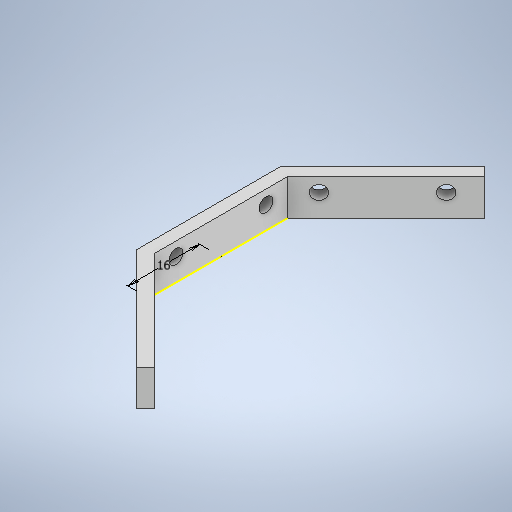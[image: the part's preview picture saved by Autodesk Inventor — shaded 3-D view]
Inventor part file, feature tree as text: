
AUTODESK INVENTOR PART (.ipt)
format: ipt  version: 2025.1 (Build 291241020, 241B)  size: 315,904 bytes
history: native  units: in
note: dims shown in document units (in); Inventor stores cm internally (conversion verified against a paired STEP export)
features: sketch x5, extrude x4
ambient origin geometry x8: Origin, YZ Plane, XZ Plane, XY Plane, X Axis, Y Axis, Z Axis, Center Point
bodies: Body1 (feature_tree)
feature tree (9):
  extrude  "Extrusion2"  Depth=0.315in
  extrude  "Extrusion7"  Depth=0.0787in
  extrude  "Extrusion8"  Depth=1.2205in
  extrude  "Extrusion9"  Depth=0.5118in
  sketch  "Sketch12"  dims[d74=0.1181in d75=0.1969in d76=0.3937in d77=0.1201in d78=0.1201in d79=0.315in d80=0.0in d81=0.5118in d82=0.1181in d83=0.1969in d84=0.3937in d85=0.1201in d86=0.1201in d87=0.315in d88=0.0in d89=0.6299in d90=0.5118in d91=0.1181in d92=0.1969in d93=0.3937in d94=0.1201in d95=0.1201in d96=0.315in d97=0.0in d98=0.6299in d14=0.0197in d15=0.0344in d16=0.0197in d17=0.0344in]
  sketch  "Sketch1"  dims[d18=0.315in d19=0.0in d64=1.2598in]
  sketch  "Sketch9"  dims[d65=1.2598in d66=0.0787in]
  sketch  "Sketch10"  dims[d67=1.2598in d70=1.2205in]
  sketch  "Sketch11"  dims[d72=0.6299in d73=0.5118in]
